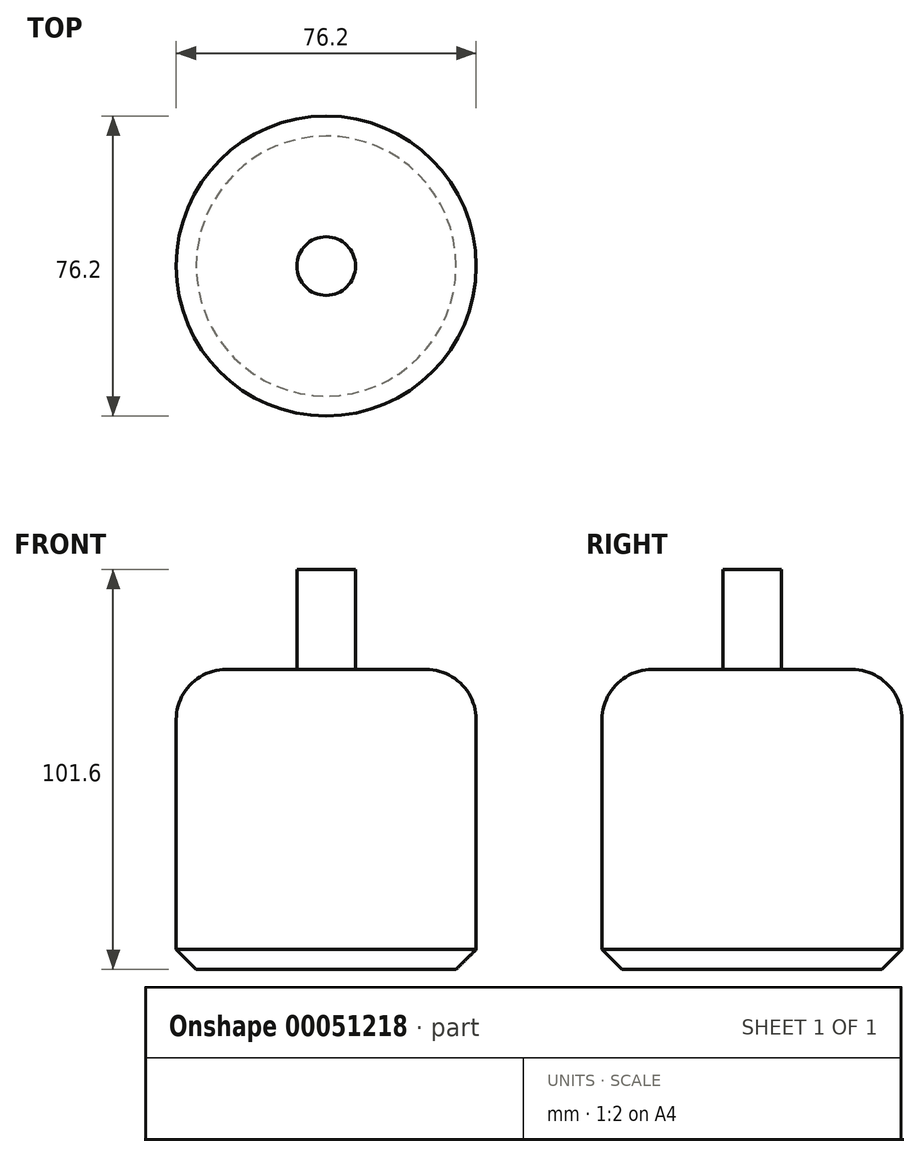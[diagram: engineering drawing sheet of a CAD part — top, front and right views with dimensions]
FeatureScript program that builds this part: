
annotation { "Feature Type Name" : "Feature", "Feature Type Description" : "" }
export const myFeature = defineFeature(function(context is Context, id is Id, definition is map)
    precondition{}
    {
        {
            var Q0;
            Q0=qCreatedBy(makeId("Top.planeOp"),FACE);
            var sketch = newSketch(context, id + "F0", { "sketchPlane" : qUnion([Q0])});
            skCircle(sketch, "E0", {"center": v(0, 0) * mm, "radius": 38.1 * mm});
            skSolve(sketch);
        }
        {
            var Q0;
            Q0=makeQuery(id+"F0.imprint","IMPRINT",FACE,{"disambiguationData":[TD([[makeQuery(id+"F0.imprint","IMPRINT",EDGE,{"derivedFrom":sQuery(id+"F0.wireOp",EDGE,"E0")}),1.0]])]});
            extrude(context, id + "F1", {"entities" : qUnion([Q0]), "depth" : 76.2 * mm});
        }
        {
            var Q0;
            Q0=makeQuery(id+"F1.opExtrude","CAP_FACE",FACE,{"disambiguationData":[OSD([sQuery(id+"F0.wireOp",EDGE,"E0")])],"isStart":false});
            var sketch = newSketch(context, id + "F4", { "sketchPlane" : qUnion([Q0])});
            skCircle(sketch, "E1", {"center": v(0, 0) * mm, "radius": 7.45 * mm});
            skSolve(sketch);
        }
        {
            var Q0;
            Q0=makeQuery(id+"F4.imprint","IMPRINT",FACE,{"disambiguationData":[TD([[makeQuery(id+"F4.imprint","IMPRINT",EDGE,{"derivedFrom":sQuery(id+"F4.wireOp",EDGE,"E1")}),1.0]])]});
            extrude(context, id + "F5", {"entities" : qUnion([Q0]), "operationType" : NewBodyOperationType.ADD, "depth" : 25.4 * mm});
        }
        {
            var Q0;
            Q0=makeQuery(id+"F1.opExtrude","CAP_EDGE",EDGE,{"disambiguationData":[OSD([sQuery(id+"F0.wireOp",EDGE,"E0")])],"isStart":false});
            fillet(context, id + "F2", {"entities" : qUnion([Q0]), "radius" : 12.7 * mm, "tangentPropagation" : true, "allowEdgeOverflow" : false});
        }
        {
            var Q0;
            Q0=makeQuery(id+"F1.opExtrude","CAP_EDGE",EDGE,{"disambiguationData":[OSD([sQuery(id+"F0.wireOp",EDGE,"E0")])],"isStart":true});
            chamfer(context, id + "F3", {"entities" : qUnion([Q0]), "width" : 5.08 * mm, "tangentPropagation" : true});
        }
    });
